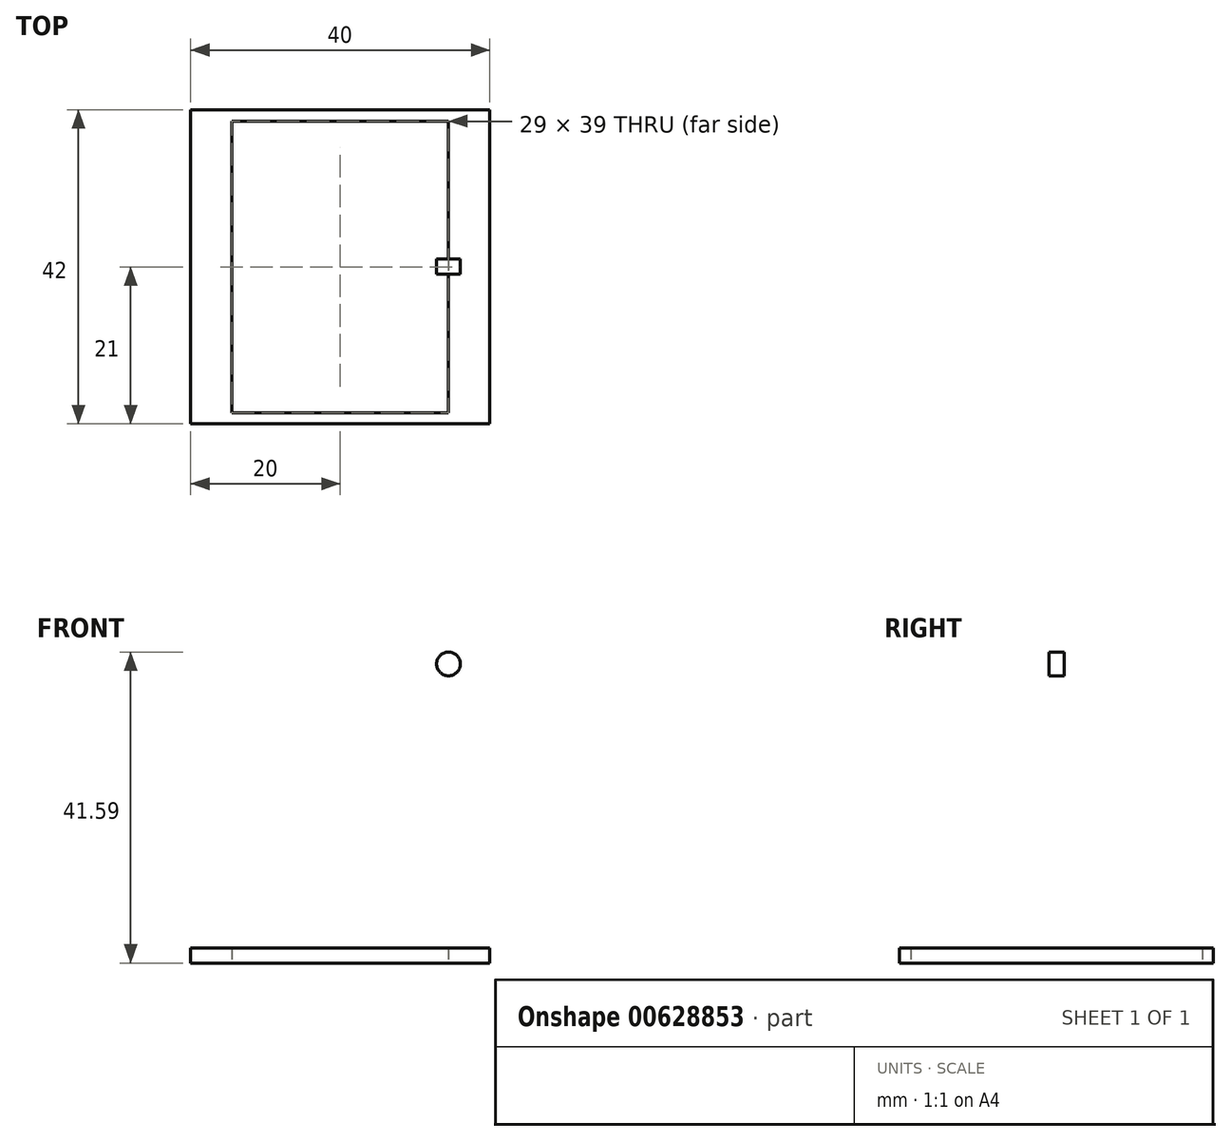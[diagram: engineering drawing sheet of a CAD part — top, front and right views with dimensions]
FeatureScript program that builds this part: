
annotation { "Feature Type Name" : "Feature", "Feature Type Description" : "" }
export const myFeature = defineFeature(function(context is Context, id is Id, definition is map)
    precondition{}
    {
        {
            var Q0;
            Q0=qCreatedBy(makeId("Top.planeOp"),FACE);
            var sketch = newSketch(context, id + "F0", { "sketchPlane" : qUnion([Q0])});
            skLineSegment(sketch, "E0.bottom", {"start": v(20, 21) * mm, "end": v(-20, 21) * mm});
            skLineSegment(sketch, "E0.top", {"start": v(20, -21) * mm, "end": v(-20, -21) * mm});
            skLineSegment(sketch, "E0.left", {"start": v(20, 21) * mm, "end": v(20, -21) * mm});
            skLineSegment(sketch, "E0.right", {"start": v(-20, 21) * mm, "end": v(-20, -21) * mm});
            skPoint(sketch, "E0.middle", {"position": v(0, 0) * mm});
            skLineSegment(sketch, "E1.bottom", {"start": v(14.5, 19.5) * mm, "end": v(-14.5, 19.5) * mm});
            skLineSegment(sketch, "E1.top", {"start": v(14.5, -19.5) * mm, "end": v(-14.5, -19.5) * mm});
            skLineSegment(sketch, "E1.left", {"start": v(14.5, 19.5) * mm, "end": v(14.5, -19.5) * mm});
            skLineSegment(sketch, "E1.right", {"start": v(-14.5, 19.5) * mm, "end": v(-14.5, -19.5) * mm});
            skSolve(sketch);
        }
        {
            var Q0;
            Q0=makeQuery(id+"F0.imprint","IMPRINT",FACE,{"disambiguationData":[TD([[makeQuery(id+"F0.imprint","IMPRINT",EDGE,{"derivedFrom":sQuery(id+"F0.wireOp",EDGE,"E0.bottom")}),1.0]])]});
            extrude(context, id + "F1", {"entities" : qUnion([Q0]), "depth" : 2 * mm, "offsetDistance" : 25 * mm});
        }
        {
            var Q0;
            Q0=makeQuery(id+"F1.opExtrude","CAP_FACE",FACE,{"disambiguationData":[OSD([sQuery(id+"F0.wireOp",EDGE,"E0.bottom"),sQuery(id+"F0.wireOp",EDGE,"E0.top"),sQuery(id+"F0.wireOp",EDGE,"E0.left"),sQuery(id+"F0.wireOp",EDGE,"E0.right"),sQuery(id+"F0.wireOp",EDGE,"E1.bottom"),sQuery(id+"F0.wireOp",EDGE,"E1.top"),sQuery(id+"F0.wireOp",EDGE,"E1.left"),sQuery(id+"F0.wireOp",EDGE,"E1.right")])],"isStart":false});
            var sketch = newSketch(context, id + "F2", { "sketchPlane" : qUnion([Q0])});
            skLineSegment(sketch, "E2.bottom", {"start": v(14.5, -1) * mm, "end": v(20, -1) * mm});
            skLineSegment(sketch, "E2.top", {"start": v(14.5, 1) * mm, "end": v(20, 1) * mm});
            skLineSegment(sketch, "E2.left", {"start": v(14.5, -1) * mm, "end": v(14.5, 1) * mm});
            skLineSegment(sketch, "E2.right", {"start": v(20, -1) * mm, "end": v(20, 1) * mm});
            skLineSegment(sketch, "E3.MirrorCS", {"start": v(-14.5, 1) * mm, "end": v(-20, 1) * mm});
            skLineSegment(sketch, "E4.MirrorCS", {"start": v(-14.5, -1) * mm, "end": v(-20, -1) * mm});
            skLineSegment(sketch, "E5.MirrorCS", {"start": v(-14.5, -1) * mm, "end": v(-14.5, 1) * mm});
            skLineSegment(sketch, "E6.MirrorCS", {"start": v(-20, -1) * mm, "end": v(-20, 1) * mm});
            skSolve(sketch);
        }
        {
            var Q0;
            Q0=makeQuery(id+"F2.imprint","IMPRINT",FACE,{"disambiguationData":[TD([[makeQuery(id+"F2.imprint","IMPRINT",EDGE,{"derivedFrom":sQuery(id+"F2.wireOp",EDGE,"E3.MirrorCS")}),1.0]])]});
            var Q1;
            Q1=makeQuery(id+"F2.imprint","IMPRINT",FACE,{"disambiguationData":[TD([[makeQuery(id+"F2.imprint","IMPRINT",EDGE,{"derivedFrom":sQuery(id+"F2.wireOp",EDGE,"E2.bottom")}),1.0]])]});
            extrude(context, id + "F3", {"entities" : qUnion([Q0, Q1]), "operationType" : NewBodyOperationType.ADD, "depth" : 2 * mm, "offsetDistance" : 25 * mm});
        }
        {
            var Q0;
            Q0=makeQuery(id+"F3.opExtrude","CAP_FACE",FACE,{"disambiguationData":[OSD([sQuery(id+"F2.wireOp",EDGE,"E3.MirrorCS"),sQuery(id+"F2.wireOp",EDGE,"E4.MirrorCS"),sQuery(id+"F2.wireOp",EDGE,"E5.MirrorCS"),sQuery(id+"F2.wireOp",EDGE,"E6.MirrorCS")])],"isStart":false});
            var sketch = newSketch(context, id + "F4", { "sketchPlane" : qUnion([Q0])});
            skLineSegment(sketch, "E7.bottom", {"start": v(-20, -1) * mm, "end": v(19.95, -1) * mm});
            skLineSegment(sketch, "E7.top", {"start": v(-20, 1.03) * mm, "end": v(19.95, 1.03) * mm});
            skLineSegment(sketch, "E7.left", {"start": v(-20, -1) * mm, "end": v(-20, 1.03) * mm});
            skLineSegment(sketch, "E7.right", {"start": v(19.95, -1) * mm, "end": v(19.95, 1.03) * mm});
            skSolve(sketch);
        }
        {
            var Q0;
            {var subQ2=sQuery(id+"F4.wireOp",EDGE,"E7.top");Q0=makeQuery(id+"F4.imprint","IMPRINT",FACE,{"disambiguationData":[TD([[makeQuery(id+"F4.imprint","IMPRINT",EDGE,{"derivedFrom":subQ2}),-1.0]])]});}
            var Q1;
            {var subQ4=makeQuery(id+"F3.opExtrude","CAP_EDGE",EDGE,{"disambiguationData":[OSD([sQuery(id+"F2.wireOp",EDGE,"E3.MirrorCS")])],"isStart":false});Q1=makeQuery(id+"F4.imprint","IMPRINT",FACE,{"disambiguationData":[TD([[makeQuery(id+"F4.imprint","IMPRINT",EDGE,{"derivedFrom":subQ4}),1.0]])]});}
            extrude(context, id + "F5", {"entities" : qUnion([Q0, Q1]), "operationType" : NewBodyOperationType.ADD, "depth" : 40 * mm, "offsetDistance" : 25 * mm});
        }
        {
            var Q0;
            Q0=makeQuery(id+"F5.boolean.opBoolean","MERGE",FACE,{"derivedFrom":[makeQuery(id+"F3.opExtrude","SWEPT_FACE",FACE,{"disambiguationData":[OSD([sQuery(id+"F2.wireOp",EDGE,"E2.bottom")])]}),makeQuery(id+"F3.opExtrude","SWEPT_FACE",FACE,{"disambiguationData":[OSD([sQuery(id+"F2.wireOp",EDGE,"E4.MirrorCS")])]}),makeQuery(id+"F5.opExtrude","SWEPT_FACE",FACE,{"disambiguationData":[OSD([sQuery(id+"F4.wireOp",EDGE,"E7.bottom")])]})]});
            var sketch = newSketch(context, id + "F6", { "sketchPlane" : qUnion([Q0])});
            skLineSegment(sketch, "E8", {"start": v(-14.5, 4) * mm, "end": v(-14.5, 40) * mm, "construction": true});
            skCircle(sketch, "E9", {"center": v(-14.5, 40) * mm, "radius": 1.6 * mm});
            skCircle(sketch, "E10.MirrorC", {"center": v(14.5, 40) * mm, "radius": 1.6 * mm});
            skSolve(sketch);
        }
        {
            var Q0;
            Q0=makeQuery(id+"F6.imprint","IMPRINT",FACE,{"disambiguationData":[TD([[makeQuery(id+"F6.imprint","IMPRINT",EDGE,{"derivedFrom":sQuery(id+"F6.wireOp",EDGE,"E9")}),1.0]])]});
            var Q1;
            Q1=makeQuery(id+"F6.imprint","IMPRINT",FACE,{"disambiguationData":[TD([[makeQuery(id+"F6.imprint","IMPRINT",EDGE,{"derivedFrom":sQuery(id+"F6.wireOp",EDGE,"E10.MirrorC")}),-1.0]])]});
            var Q2;
            Q2=sQuery(id+"F6.wireOp",EDGE,"E9");
            var Q3;
            Q3=sQuery(id+"F6.wireOp",EDGE,"E10.MirrorC");
            extrude(context, id + "F7", {"entities" : qUnion([Q0, Q1]), "operationType" : NewBodyOperationType.REMOVE, "surfaceEntities" : qUnion([Q2, Q3]), "oppositeDirection" : true, "depth" : 3 * mm, "offsetDistance" : 25 * mm});
        }
    });
